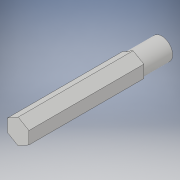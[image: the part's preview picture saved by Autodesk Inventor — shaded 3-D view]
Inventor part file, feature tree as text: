
AUTODESK INVENTOR PART (.ipt)
format: ipt  version: 2018 (Build 220112000, 112)  size: 112,128 bytes
history: native  units: in
note: dims shown in document units (in); Inventor stores cm internally (conversion verified against a paired STEP export)
features: extrude x2, sketch x2
ambient origin geometry x8: Origin, YZ Plane, XZ Plane, XY Plane, X Axis, Y Axis, Z Axis, Center Point
bodies: Solid1 (feature_tree)
feature tree (4):
  extrude  "Extrusion1"  Depth=2.0in
  extrude  "Extrusion3"  [1 undecoded]
  sketch  "Sketch1"  dims[d0=2.0in d1=0.0in d5=0.1875in]
  sketch  "Sketch3"  dims[d13=0.5in d14=0.0in]
note: 1 required parameter value undecoded (feature->parameter linkage not recoverable at this tier; creation-order binding heuristic only, values carry confidence <= 0.55)
